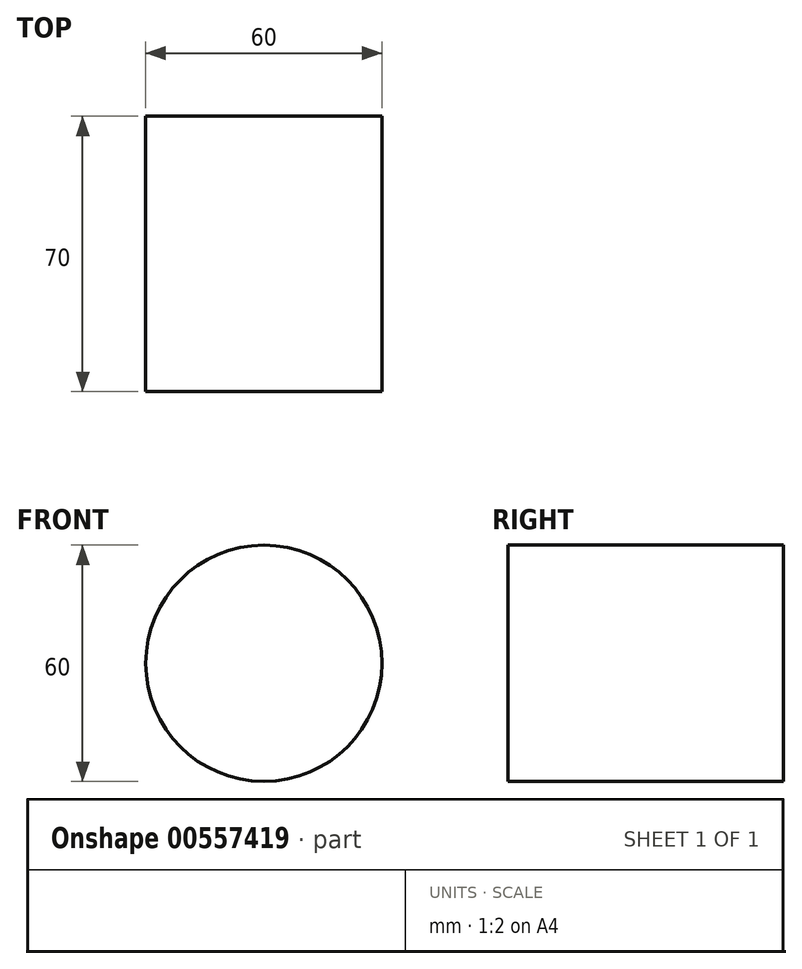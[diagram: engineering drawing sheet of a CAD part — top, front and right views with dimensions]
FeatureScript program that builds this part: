
annotation { "Feature Type Name" : "Feature", "Feature Type Description" : "" }
export const myFeature = defineFeature(function(context is Context, id is Id, definition is map)
    precondition{}
    {
        {
            var Q0;
            Q0=qCreatedBy(makeId("Front.planeOp"),FACE);
            var sketch = newSketch(context, id + "F0", { "sketchPlane" : qUnion([Q0])});
            skCircle(sketch, "E0", {"center": v(0, 0) * mm, "radius": 30 * mm});
            skSolve(sketch);
        }
        {
            var Q0;
            Q0=makeQuery(id+"F0.imprint","IMPRINT",FACE,{"disambiguationData":[TD([[makeQuery(id+"F0.imprint","IMPRINT",EDGE,{"derivedFrom":sQuery(id+"F0.wireOp",EDGE,"E0")}),1.0]])]});
            extrude(context, id + "F1", {"entities" : qUnion([Q0]), "depth" : 70 * mm, "offsetDistance" : 25 * mm});
        }
    });
